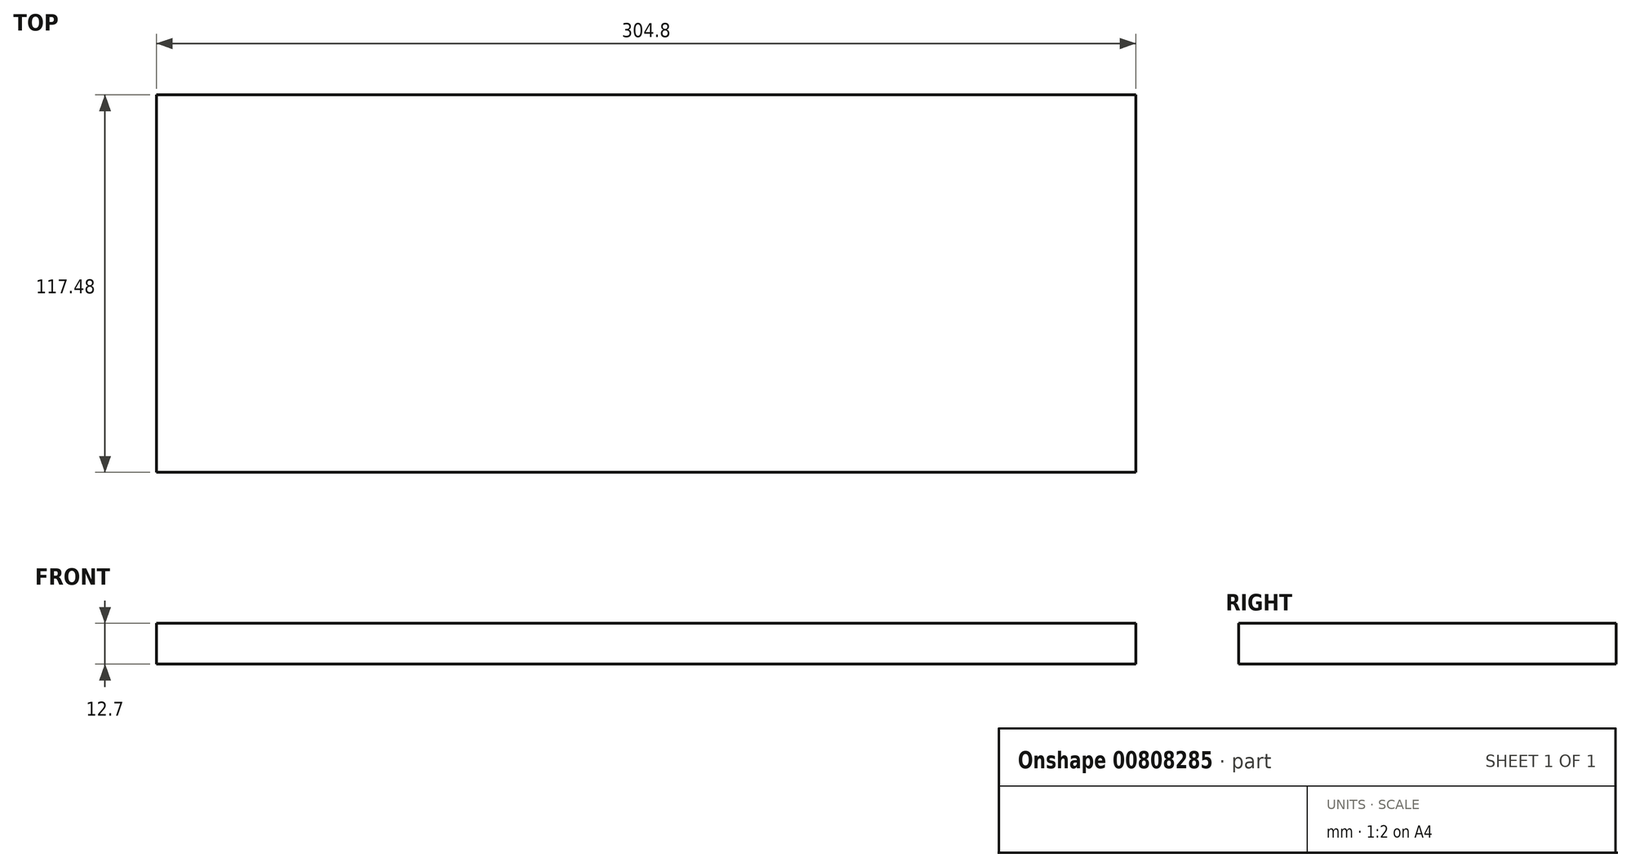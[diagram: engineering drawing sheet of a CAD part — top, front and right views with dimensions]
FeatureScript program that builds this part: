
annotation { "Feature Type Name" : "Feature", "Feature Type Description" : "" }
export const myFeature = defineFeature(function(context is Context, id is Id, definition is map)
    precondition{}
    {
        {
            var Q0;
            Q0=qCreatedBy(makeId("Top.planeOp"),FACE);
            var sketch = newSketch(context, id + "F0", { "sketchPlane" : qUnion([Q0])});
            skLineSegment(sketch, "E0.bottom", {"start": v(152.4, -58.74) * mm, "end": v(-152.4, -58.74) * mm});
            skLineSegment(sketch, "E0.top", {"start": v(152.4, 58.74) * mm, "end": v(-152.4, 58.74) * mm});
            skLineSegment(sketch, "E0.left", {"start": v(152.4, -58.74) * mm, "end": v(152.4, 58.74) * mm});
            skLineSegment(sketch, "E0.right", {"start": v(-152.4, -58.74) * mm, "end": v(-152.4, 58.74) * mm});
            skPoint(sketch, "E0.middle", {"position": v(0, 0) * mm});
            skSolve(sketch);
        }
        {
            var Q0;
            Q0=qSketchRegion(id+"F0",true);
            extrude(context, id + "F1", {"entities" : qUnion([Q0]), "depth" : 12.7 * mm, "offsetDistance" : 25 * mm});
        }
    });
